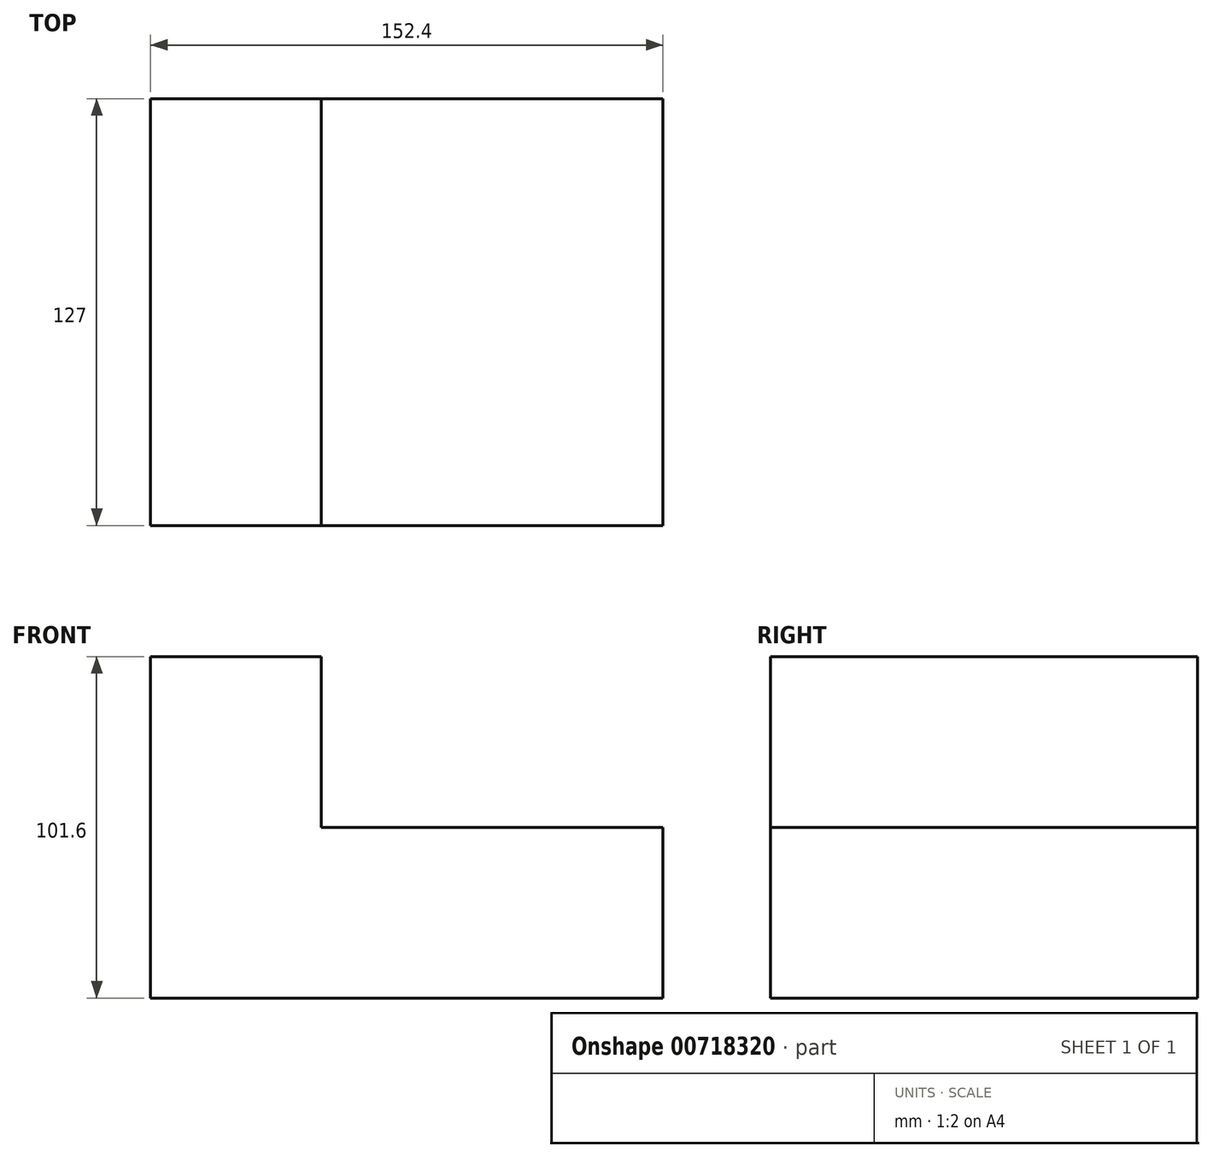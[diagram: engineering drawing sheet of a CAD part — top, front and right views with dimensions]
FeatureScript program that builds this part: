
annotation { "Feature Type Name" : "Feature", "Feature Type Description" : "" }
export const myFeature = defineFeature(function(context is Context, id is Id, definition is map)
    precondition{}
    {
        {
            var Q0;
            Q0=qCreatedBy(makeId("Front.planeOp"),FACE);
            var sketch = newSketch(context, id + "F0", { "sketchPlane" : qUnion([Q0])});
            skLineSegment(sketch, "E0", {"start": v(-98.33, -75.11) * mm, "end": v(54.07, -75.11) * mm});
            skLineSegment(sketch, "E1", {"start": v(54.07, -75.11) * mm, "end": v(54.07, -24.31) * mm});
            skLineSegment(sketch, "E2", {"start": v(54.07, -24.31) * mm, "end": v(-47.53, -24.31) * mm});
            skLineSegment(sketch, "E3", {"start": v(-47.53, -24.31) * mm, "end": v(-47.53, 26.49) * mm});
            skLineSegment(sketch, "E4", {"start": v(-47.53, 26.49) * mm, "end": v(-98.33, 26.49) * mm});
            skLineSegment(sketch, "E5", {"start": v(-98.33, 26.49) * mm, "end": v(-98.33, -75.11) * mm});
            skLineSegment(sketch, "E6", {"start": v(-98.33, -75.11) * mm, "end": v(-98.33, -9.37) * mm});
            skSolve(sketch);
        }
        {
            var Q0;
            Q0=makeQuery(id+"F0.imprint","IMPRINT",FACE,{"disambiguationData":[TD([[makeQuery(id+"F0.imprint","IMPRINT",EDGE,{"derivedFrom":sQuery(id+"F0.wireOp",EDGE,"E0")}),1.0]])]});
            extrude(context, id + "F1", {"entities" : qUnion([Q0]), "depth" : 127 * mm, "offsetDistance" : 25.4 * mm});
        }
    });
